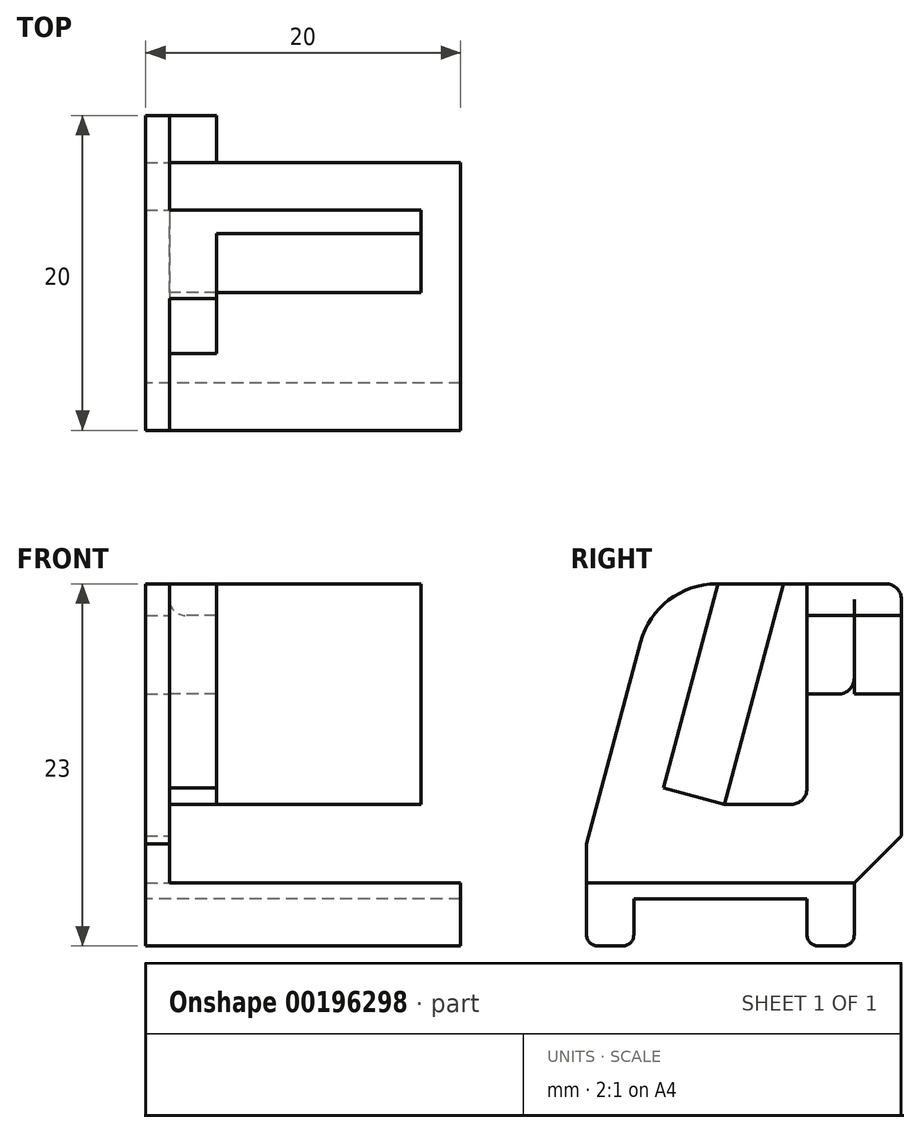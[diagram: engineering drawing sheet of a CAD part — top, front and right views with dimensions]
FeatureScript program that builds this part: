
annotation { "Feature Type Name" : "Feature", "Feature Type Description" : "" }
export const myFeature = defineFeature(function(context is Context, id is Id, definition is map)
    precondition{}
    {
        {
            var Q0;
            Q0=qCreatedBy(makeId("Top.planeOp"),FACE);
            var sketch = newSketch(context, id + "F0", { "sketchPlane" : qUnion([Q0])});
            skLineSegment(sketch, "E0.bottom", {"start": v(9.25, 8.5) * mm, "end": v(-9.25, 8.5) * mm});
            skLineSegment(sketch, "E0.top", {"start": v(9.25, -8.5) * mm, "end": v(-9.25, -8.5) * mm});
            skLineSegment(sketch, "E0.left", {"start": v(9.25, 8.5) * mm, "end": v(9.25, -8.5) * mm});
            skLineSegment(sketch, "E0.right", {"start": v(-9.25, 8.5) * mm, "end": v(-9.25, -8.5) * mm});
            skPoint(sketch, "E0.middle", {"position": v(0, 0) * mm});
            skSolve(sketch);
        }
        {
            var Q0;
            Q0 = qSketchRegion(id + "F0", true);
            extrude(context, id + "F1", {"entities" : qUnion([Q0]), "depth" : 1 * mm});
        }
        {
            var Q0;
            Q0=makeQuery(id+"F1.opExtrude","SWEPT_FACE",FACE,{"disambiguationData":[OSD([sQuery(id+"F0.wireOp",EDGE,"E0.right")])]});
            var sketch = newSketch(context, id + "F2", { "sketchPlane" : qUnion([Q0])});
            skLineSegment(sketch, "E1", {"start": v(4.08, 20) * mm, "end": v(-5.5, 20) * mm});
            skLineSegment(sketch, "E2", {"start": v(-5.5, 20) * mm, "end": v(-0.4, 1) * mm, "construction": true});
            skLineSegment(sketch, "E3", {"start": v(8.5, 1) * mm, "end": v(8.5, 3.5) * mm});
            skLineSegment(sketch, "E4", {"start": v(8.5, 3.5) * mm, "end": v(4.08, 20) * mm});
            skLineSegment(sketch, "E5", {"start": v(-8.5, 1) * mm, "end": v(-11.5, 4) * mm});
            skLineSegment(sketch, "E6", {"start": v(-5.5, 20) * mm, "end": v(-11.5, 20) * mm});
            skLineSegment(sketch, "E7", {"start": v(-11.5, 4) * mm, "end": v(-11.5, 20) * mm});
            skLineSegment(sketch, "E8.bottom", {"start": v(-5.5, 18) * mm, "end": v(-8.5, 18) * mm});
            skLineSegment(sketch, "E8.top", {"start": v(-5.5, 13) * mm, "end": v(-8.5, 13) * mm});
            skLineSegment(sketch, "E8.left", {"start": v(-5.5, 18) * mm, "end": v(-5.5, 13) * mm});
            skLineSegment(sketch, "E8.right", {"start": v(-8.5, 18) * mm, "end": v(-8.5, 13) * mm});
            skSolve(sketch);
        }
        {
            var Q0;
            Q0=makeQuery(id+"F2.imprint","IMPRINT",FACE,{"disambiguationData":[TD([[makeQuery(id+"F2.imprint","IMPRINT",EDGE,{"derivedFrom":sQuery(id+"F2.wireOp",EDGE,"E1")}),1.0]])]});
            var Q1;
            {var subQ0=sQuery(id+"F0.wireOp",EDGE,"E0.right");Q1=makeQuery(id+"F2.imprint","IMPRINT",FACE,{"disambiguationData":[TD([[makeQuery(id+"F2.imprint","IMPRINT",EDGE,{"derivedFrom":makeQuery(id+"F1.opExtrude","CAP_EDGE",EDGE,{"disambiguationData":[OSD([subQ0])],"isStart":true})}),1.0]])]});}
            extrude(context, id + "F3", {"entities" : qUnion([Q0, Q1]), "operationType" : NewBodyOperationType.ADD, "depth" : 1.5 * mm});
        }
        {
            var Q0;
            Q0=makeQuery(id+"F3.opExtrude","CAP_FACE",FACE,{"disambiguationData":[OSD([sQuery(id+"F0.wireOp",EDGE,"E0.bottom"),sQuery(id+"F0.wireOp",EDGE,"E0.top"),sQuery(id+"F0.wireOp",EDGE,"E0.right"),sQuery(id+"F2.wireOp",EDGE,"4b1GKvsR-eN0K-ExlU-scpf-oMq5W9asBjAQ"),sQuery(id+"F2.wireOp",EDGE,"E1"),sQuery(id+"F2.wireOp",EDGE,"E2"),sQuery(id+"F2.wireOp",EDGE,"E3"),sQuery(id+"F2.wireOp",EDGE,"E4"),sQuery(id+"F2.wireOp",EDGE,"E5"),sQuery(id+"F2.wireOp",EDGE,"0JAiiQl1-8YML-yuAu-NIjA-4Og0W7mxUHpT")])],"isStart":true});
            var sketch = newSketch(context, id + "F4", { "sketchPlane" : qUnion([Q0])});
            skLineSegment(sketch, "E9", {"start": v(4, 20) * mm, "end": v(0.25, 6) * mm});
            skLineSegment(sketch, "E10", {"start": v(0.25, 6) * mm, "end": v(5.5, 6) * mm});
            skLineSegment(sketch, "E11", {"start": v(5.5, 20) * mm, "end": v(4, 20) * mm});
            skLineSegment(sketch, "E12", {"start": v(5.5, 20) * mm, "end": v(5.5, 6) * mm});
            skLineSegment(sketch, "E13.bottom", {"start": v(11.5, 20) * mm, "end": v(8.5, 20) * mm});
            skLineSegment(sketch, "E13.top", {"start": v(11.5, 13) * mm, "end": v(8.5, 13) * mm});
            skLineSegment(sketch, "E13.left", {"start": v(11.5, 20) * mm, "end": v(11.5, 13) * mm});
            skLineSegment(sketch, "E13.right", {"start": v(8.5, 20) * mm, "end": v(8.5, 13) * mm});
            skSolve(sketch);
        }
        {
            var Q0;
            Q0=makeQuery(id+"F4.imprint","IMPRINT",FACE,{"disambiguationData":[TD([[makeQuery(id+"F4.imprint","IMPRINT",EDGE,{"derivedFrom":sQuery(id+"F4.wireOp",EDGE,"E9")}),1.0]])]});
            extrude(context, id + "F5", {"entities" : qUnion([Q0]), "operationType" : NewBodyOperationType.ADD, "depth" : 16 * mm});
        }
        {
            var Q0;
            {var subQ9=sQuery(id+"F4.wireOp",EDGE,"E9");Q0=makeQuery(id+"F4.imprint","IMPRINT",FACE,{"disambiguationData":[TD([[makeQuery(id+"F4.imprint","IMPRINT",EDGE,{"derivedFrom":subQ9}),-1.0]])]});}
            var sketch = newSketch(context, id + "F6", { "sketchPlane" : qUnion([Q0])});
            skLineSegment(sketch, "E14", {"start": v(-0.14, 20) * mm, "end": v(4, 20) * mm});
            skLineSegment(sketch, "E15", {"start": v(4, 20) * mm, "end": v(0.25, 6) * mm});
            skLineSegment(sketch, "E16", {"start": v(0.25, 6) * mm, "end": v(-3.61, 7.04) * mm});
            skLineSegment(sketch, "E17", {"start": v(-3.61, 7.04) * mm, "end": v(-0.14, 20) * mm});
            skLineSegment(sketch, "E18.bottom", {"start": v(11.5, 18) * mm, "end": v(8.5, 18) * mm});
            skLineSegment(sketch, "E18.top", {"start": v(11.5, 13) * mm, "end": v(8.5, 13) * mm});
            skLineSegment(sketch, "E18.left", {"start": v(11.5, 18) * mm, "end": v(11.5, 13) * mm});
            skLineSegment(sketch, "E18.right", {"start": v(8.5, 18) * mm, "end": v(8.5, 13) * mm});
            skSolve(sketch);
        }
        {
            var Q0;
            Q0 = qSketchRegion(id + "F6", true);
            extrude(context, id + "F7", {"entities" : qUnion([Q0]), "operationType" : NewBodyOperationType.ADD, "depth" : 3 * mm});
        }
        {
            var Q0;
            Q0=makeQuery(id+"F1.opExtrude","CAP_EDGE",EDGE,{"disambiguationData":[OSD([sQuery(id+"F0.wireOp",EDGE,"E0.right")])],"isStart":false});
            var Q1;
            Q1=makeQuery(id+"F5.opExtrude","CAP_EDGE",EDGE,{"disambiguationData":[OSD([sQuery(id+"F4.wireOp",EDGE,"E10")])],"isStart":true});
            var Q2;
            Q2=makeQuery(id+"F5.opExtrude","SWEPT_EDGE",EDGE,{"disambiguationData":[OSD([sQuery(id+"F4.wireOp",EDGE,"E10"),sQuery(id+"F4.wireOp",EDGE,"E12")])]});
            var Q3;
            {var subQ1=sQuery(id+"F2.wireOp",EDGE,"E8.top");var subQ2=sQuery(id+"F4.wireOp",EDGE,"E12");Q3=makeQuery(id+"F5.boolean.opBoolean","SPLIT",EDGE,{"disambiguationData":[TD([makeQuery(id+"F3.opExtrude","SWEPT_FACE",FACE,{"disambiguationData":[OSD([subQ1])]})])],"derivedFrom":makeQuery(id+"F5.opExtrude","CAP_EDGE",EDGE,{"disambiguationData":[OSD([subQ2])],"isStart":true})});}
            var Q4;
            {var subQ0=sQuery(id+"F2.wireOp",EDGE,"E8.bottom");var subQ4=sQuery(id+"F4.wireOp",EDGE,"E12");Q4=makeQuery(id+"F5.boolean.opBoolean","SPLIT",EDGE,{"disambiguationData":[TD([makeQuery(id+"F3.opExtrude","SWEPT_FACE",FACE,{"disambiguationData":[OSD([subQ0])]})])],"derivedFrom":makeQuery(id+"F5.opExtrude","CAP_EDGE",EDGE,{"disambiguationData":[OSD([subQ4])],"isStart":true})});}
            var Q5;
            Q5=makeQuery(id+"F7.opExtrude","CAP_EDGE",EDGE,{"disambiguationData":[OSD([sQuery(id+"F6.wireOp",EDGE,"E18.bottom")])],"isStart":true});
            var Q6;
            Q6=makeQuery(id+"F7.opExtrude","CAP_EDGE",EDGE,{"disambiguationData":[OSD([sQuery(id+"F6.wireOp",EDGE,"E18.right")])],"isStart":true});
            var Q7;
            Q7=makeQuery(id+"F3.opExtrude","SWEPT_EDGE",EDGE,{"disambiguationData":[OSD([sQuery(id+"F2.wireOp",EDGE,"E8.top"),sQuery(id+"F2.wireOp",EDGE,"E8.right")])]});
            var Q8;
            Q8=makeQuery(id+"F7.opExtrude","CAP_EDGE",EDGE,{"disambiguationData":[OSD([sQuery(id+"F6.wireOp",EDGE,"E16")])],"isStart":true});
            var Q9;
            Q9=makeQuery(id+"F3.opExtrude","SWEPT_EDGE",EDGE,{"disambiguationData":[OSD([sQuery(id+"F2.wireOp",EDGE,"E6"),sQuery(id+"F2.wireOp",EDGE,"E7")])]});
            fillet(context, id + "F8", {"entities" : qUnion([Q0, Q1, Q2, Q3, Q4, Q5, Q6, Q7, Q8, Q9]), "radius" : 1 * mm, "tangentPropagation" : true, "allowEdgeOverflow" : false});
        }
        {
            var Q0;
            Q0=makeQuery(id+"F3.opExtrude","SWEPT_EDGE",EDGE,{"disambiguationData":[OSD([sQuery(id+"F2.wireOp",EDGE,"E1"),sQuery(id+"F2.wireOp",EDGE,"E4")])]});
            fillet(context, id + "F9", {"entities" : qUnion([Q0]), "radius" : 5 * mm, "tangentPropagation" : true, "allowEdgeOverflow" : false});
        }
        {
            var Q0;
            Q0=makeQuery(id+"F3.opExtrude","CAP_FACE",FACE,{"disambiguationData":[OSD([sQuery(id+"F0.wireOp",EDGE,"E0.bottom"),sQuery(id+"F0.wireOp",EDGE,"E0.top"),sQuery(id+"F0.wireOp",EDGE,"E0.right"),sQuery(id+"F2.wireOp",EDGE,"E1"),sQuery(id+"F2.wireOp",EDGE,"E3"),sQuery(id+"F2.wireOp",EDGE,"E4"),sQuery(id+"F2.wireOp",EDGE,"E5"),sQuery(id+"F2.wireOp",EDGE,"E6"),sQuery(id+"F2.wireOp",EDGE,"E7"),sQuery(id+"F2.wireOp",EDGE,"E8.bottom"),sQuery(id+"F2.wireOp",EDGE,"E8.top"),sQuery(id+"F2.wireOp",EDGE,"E8.left"),sQuery(id+"F2.wireOp",EDGE,"E8.right")])],"isStart":false});
            var sketch = newSketch(context, id + "F10", { "sketchPlane" : qUnion([Q0])});
            skLineSegment(sketch, "E19", {"start": v(-8.5, 0) * mm, "end": v(-8.5, -3) * mm});
            skLineSegment(sketch, "E20", {"start": v(-8.5, -3) * mm, "end": v(-5.5, -3) * mm});
            skLineSegment(sketch, "E21", {"start": v(-5.5, -3) * mm, "end": v(-5.5, 0) * mm});
            skLineSegment(sketch, "E22", {"start": v(8.5, 0) * mm, "end": v(8.5, -3) * mm});
            skLineSegment(sketch, "E23", {"start": v(8.5, -3) * mm, "end": v(5.5, -3) * mm});
            skLineSegment(sketch, "E24", {"start": v(5.5, -3) * mm, "end": v(5.5, 0) * mm});
            skSolve(sketch);
        }
        {
            var Q0;
            {var subQ0=sQuery(id+"F10.wireOp",EDGE,"E19");Q0=makeQuery(id+"F10.imprint","IMPRINT",FACE,{"disambiguationData":[TD([[makeQuery(id+"F10.imprint","IMPRINT",EDGE,{"derivedFrom":subQ0}),1.0]])]});}
            var Q1;
            {var subQ0=sQuery(id+"F10.wireOp",EDGE,"E22");Q1=makeQuery(id+"F10.imprint","IMPRINT",FACE,{"disambiguationData":[TD([[makeQuery(id+"F10.imprint","IMPRINT",EDGE,{"derivedFrom":subQ0}),-1.0]])]});}
            var Q2;
            Q2=makeQuery(id+"F1.opExtrude","SWEPT_FACE",FACE,{"disambiguationData":[OSD([sQuery(id+"F0.wireOp",EDGE,"E0.left")])]});
            extrude(context, id + "F11", {"entities" : qUnion([Q0, Q1]), "operationType" : NewBodyOperationType.ADD, "endBound" : BoundingType.UP_TO_SURFACE, "oppositeDirection" : true, "endBoundEntityFace" : qUnion([Q2]), "depth" : 25 * mm});
        }
        {
            var Q0;
            Q0=makeQuery(id+"F11.opExtrude","SWEPT_EDGE",EDGE,{"disambiguationData":[OSD([sQuery(id+"F10.wireOp",EDGE,"E22"),sQuery(id+"F10.wireOp",EDGE,"E23")])]});
            var Q1;
            Q1=makeQuery(id+"F11.opExtrude","SWEPT_EDGE",EDGE,{"disambiguationData":[OSD([sQuery(id+"F10.wireOp",EDGE,"E23"),sQuery(id+"F10.wireOp",EDGE,"E24")])]});
            var Q2;
            Q2=makeQuery(id+"F11.opExtrude","SWEPT_EDGE",EDGE,{"disambiguationData":[OSD([sQuery(id+"F10.wireOp",EDGE,"E20"),sQuery(id+"F10.wireOp",EDGE,"E21")])]});
            var Q3;
            Q3=makeQuery(id+"F11.opExtrude","SWEPT_EDGE",EDGE,{"disambiguationData":[OSD([sQuery(id+"F10.wireOp",EDGE,"E19"),sQuery(id+"F10.wireOp",EDGE,"E20")])]});
            fillet(context, id + "F12", {"entities" : qUnion([Q0, Q1, Q2, Q3]), "radius" : .7 * mm, "tangentPropagation" : true, "allowEdgeOverflow" : false});
        }
    });
